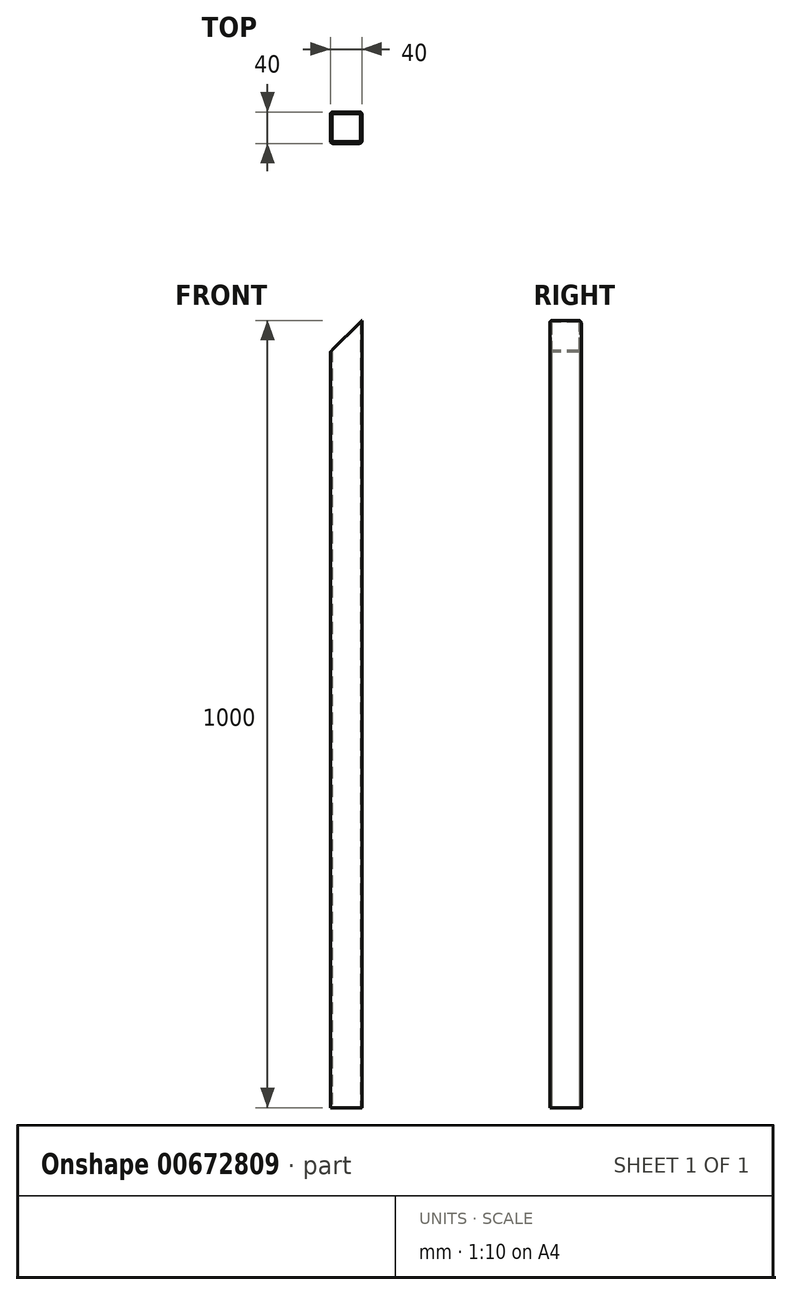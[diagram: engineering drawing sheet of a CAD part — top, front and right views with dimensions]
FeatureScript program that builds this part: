
annotation { "Feature Type Name" : "Feature", "Feature Type Description" : "" }
export const myFeature = defineFeature(function(context is Context, id is Id, definition is map)
    precondition{}
    {
        {
            var Q0;
            Q0=qCreatedBy(makeId("Top.planeOp"),FACE);
            var sketch = newSketch(context, id + "F0", { "sketchPlane" : qUnion([Q0])});
            skLineSegment(sketch, "E0.bottom", {"start": v(-17, 20) * mm, "end": v(17, 20) * mm});
            skLineSegment(sketch, "E0.top", {"start": v(-17, -20) * mm, "end": v(17, -20) * mm});
            skLineSegment(sketch, "E0.left", {"start": v(-20, 17) * mm, "end": v(-20, -17) * mm});
            skLineSegment(sketch, "E0.right", {"start": v(20, 17) * mm, "end": v(20, -17) * mm});
            skPoint(sketch, "E0.middle", {"position": v(0, 0) * mm});
            skPoint(sketch, "E1.visualSharp", {"position": v(-20, 20) * mm});
            skArc(sketch, "E1.filletArc", {"start": v(-17, 20) * mm, "mid": v(-19.12, 19.12) * mm, "end": v(-20, 17) * mm});
            skPoint(sketch, "E2.visualSharp", {"position": v(20, 20) * mm});
            skArc(sketch, "E2.filletArc", {"start": v(20, 17) * mm, "mid": v(19.12, 19.12) * mm, "end": v(17, 20) * mm});
            skPoint(sketch, "E3.visualSharp", {"position": v(20, -20) * mm});
            skArc(sketch, "E3.filletArc", {"start": v(17, -20) * mm, "mid": v(19.12, -19.12) * mm, "end": v(20, -17) * mm});
            skPoint(sketch, "E4.visualSharp", {"position": v(-20, -20) * mm});
            skArc(sketch, "E4.filletArc", {"start": v(-20, -17) * mm, "mid": v(-19.12, -19.12) * mm, "end": v(-17, -20) * mm});
            skArc(sketch, "E5.0", {"start": v(-17, 18) * mm, "mid": v(-17.7, 17.7) * mm, "end": v(-18, 17) * mm});
            skLineSegment(sketch, "E5.1", {"start": v(-18, 17) * mm, "end": v(-18, -17) * mm});
            skLineSegment(sketch, "E5.2", {"start": v(-17, 18) * mm, "end": v(17, 18) * mm});
            skArc(sketch, "E5.3", {"start": v(-18, -17) * mm, "mid": v(-17.7, -17.7) * mm, "end": v(-17, -18) * mm});
            skArc(sketch, "E5.4", {"start": v(18, 17) * mm, "mid": v(17.7, 17.7) * mm, "end": v(17, 18) * mm});
            skLineSegment(sketch, "E5.5", {"start": v(18, 17) * mm, "end": v(18, -17) * mm});
            skArc(sketch, "E5.6", {"start": v(17, -18) * mm, "mid": v(17.7, -17.7) * mm, "end": v(18, -17) * mm});
            skLineSegment(sketch, "E5.7", {"start": v(-17, -18) * mm, "end": v(17, -18) * mm});
            skSolve(sketch);
        }
        {
            var Q0;
            Q0=makeQuery(id+"F0.imprint","IMPRINT",FACE,{"disambiguationData":[TD([[makeQuery(id+"F0.imprint","IMPRINT",EDGE,{"derivedFrom":sQuery(id+"F0.wireOp",EDGE,"E0.bottom")}),-1.0]])]});
            extrude(context, id + "F1", {"entities" : qUnion([Q0]), "endBound" : BoundingType.SYMMETRIC, "depth" : 1000 * mm, "offsetDistance" : 25 * mm});
        }
        {
            var Q0;
            Q0=qCreatedBy(makeId("Front.planeOp"),FACE);
            var sketch = newSketch(context, id + "F2", { "sketchPlane" : qUnion([Q0])});
            skLineSegment(sketch, "E6.0", {"start": v(-20, 500) * mm, "end": v(-20, 460) * mm});
            skLineSegment(sketch, "E7.0", {"start": v(-20, 500) * mm, "end": v(20, 500) * mm});
            skPoint(sketch, "E8.orphan", {"position": v(-17, 500) * mm});
            skLineSegment(sketch, "E9.0", {"start": v(20, 500) * mm, "end": v(20, -500) * mm});
            skPoint(sketch, "E10.orphan", {"position": v(17, 500) * mm});
            skLineSegment(sketch, "E11", {"start": v(20, 500) * mm, "end": v(-20, 460) * mm});
            skPoint(sketch, "E12.orphan", {"position": v(-20, -500) * mm});
            skSolve(sketch);
        }
        {
            var Q0;
            Q0=makeQuery(id+"F2.imprint","IMPRINT",FACE,{"disambiguationData":[TD([[makeQuery(id+"F2.imprint","IMPRINT",EDGE,{"derivedFrom":sQuery(id+"F2.wireOp",EDGE,"E6.0")}),1.0]])]});
            extrude(context, id + "F3", {"entities" : qUnion([Q0]), "operationType" : NewBodyOperationType.REMOVE, "endBound" : BoundingType.THROUGH_ALL, "oppositeDirection" : true, "depth" : 25 * mm, "offsetDistance" : 25 * mm, "hasSecondDirection" : true, "secondDirectionBound" : SecondDirectionBoundingType.THROUGH_ALL, "secondDirectionOppositeDirection" : false, "secondDirectionDepth" : 25 * mm});
        }
    });
